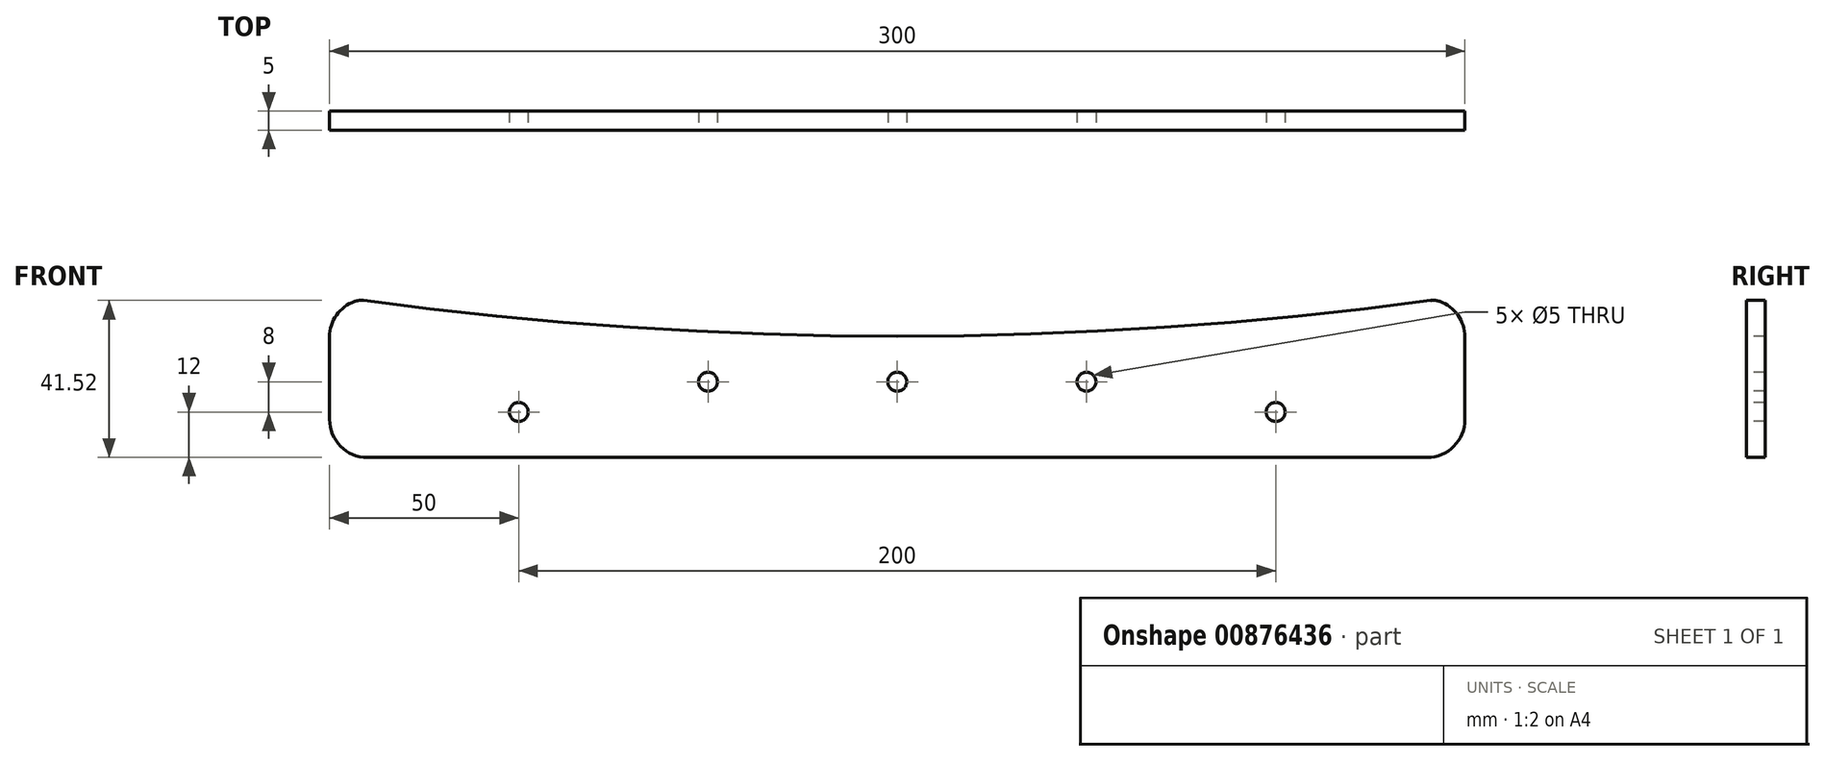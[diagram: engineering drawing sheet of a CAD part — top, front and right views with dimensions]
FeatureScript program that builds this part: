
annotation { "Feature Type Name" : "Feature", "Feature Type Description" : "" }
export const myFeature = defineFeature(function(context is Context, id is Id, definition is map)
    precondition{}
    {
        {
            var Q0;
            Q0=qCreatedBy(makeId("Front.planeOp"),FACE);
            var sketch = newSketch(context, id + "F0", { "sketchPlane" : qUnion([Q0])});
            skLineSegment(sketch, "E0", {"start": v(0, 0) * mm, "end": v(150, 0) * mm});
            skLineSegment(sketch, "E1", {"start": v(150, 0) * mm, "end": v(150, 40) * mm});
            skLineSegment(sketch, "E2", {"start": v(150, 40) * mm, "end": v(50.33, 60) * mm});
            skLineSegment(sketch, "E3", {"start": v(0, 70.22) * mm, "end": v(0, 0) * mm, "construction": true});
            skArc(sketch, "E4", {"start": v(50.33, 60) * mm, "mid": v(25.29, 63.75) * mm, "end": v(0, 65) * mm});
            skLineSegment(sketch, "E5", {"start": v(0, 65) * mm, "end": v(29, 65) * mm, "construction": true});
            skArc(sketch, "E6.MirrorCS", {"start": v(-50.33, 60) * mm, "mid": v(-25.29, 63.75) * mm, "end": v(0, 65) * mm});
            skLineSegment(sketch, "E7.MirrorCS", {"start": v(-150, 40) * mm, "end": v(-50.33, 60) * mm});
            skLineSegment(sketch, "E8.MirrorCS", {"start": v(-150, 0) * mm, "end": v(-150, 40) * mm});
            skLineSegment(sketch, "E9.MirrorCS", {"start": v(0, 0) * mm, "end": v(-150, 0) * mm});
            skSolve(sketch);
        }
        {
            var Q0;
            Q0=makeQuery(id+"F0.imprint","IMPRINT",FACE,{"disambiguationData":[TD([[makeQuery(id+"F0.imprint","IMPRINT",EDGE,{"derivedFrom":sQuery(id+"F0.wireOp",EDGE,"E0")}),1.0]])]});
            extrude(context, id + "F1", {"entities" : qUnion([Q0]), "depth" : 5 * mm, "offsetDistance" : 25 * mm});
        }
        {
            var Q0;
            Q0=makeQuery(id+"F1.opExtrude","SWEPT_EDGE",EDGE,{"disambiguationData":[OSD([sQuery(id+"F0.wireOp",EDGE,"E1"),sQuery(id+"F0.wireOp",EDGE,"E2")])]});
            var Q1;
            Q1=makeQuery(id+"F1.opExtrude","SWEPT_EDGE",EDGE,{"disambiguationData":[OSD([sQuery(id+"F0.wireOp",EDGE,"E7.MirrorCS"),sQuery(id+"F0.wireOp",EDGE,"E8.MirrorCS")])]});
            fillet(context, id + "F2", {"entities" : qUnion([Q0, Q1]), "radius" : 10 * mm, "tangentPropagation" : true, "allowEdgeOverflow" : false});
        }
        {
            var Q0;
            Q0=makeQuery(id+"F1.opExtrude","SWEPT_EDGE",EDGE,{"disambiguationData":[OSD([sQuery(id+"F0.wireOp",EDGE,"E8.MirrorCS"),sQuery(id+"F0.wireOp",EDGE,"E9.MirrorCS")])]});
            var Q1;
            Q1=makeQuery(id+"F1.opExtrude","SWEPT_EDGE",EDGE,{"disambiguationData":[OSD([sQuery(id+"F0.wireOp",EDGE,"E0"),sQuery(id+"F0.wireOp",EDGE,"E1")])]});
            fillet(context, id + "F3", {"entities" : qUnion([Q0, Q1]), "radius" : 10 * mm, "tangentPropagation" : true, "allowEdgeOverflow" : false});
        }
        {
            var Q0;
            Q0=makeQuery(id+"F1.opExtrude","CAP_FACE",FACE,{"disambiguationData":[OSD([sQuery(id+"F0.wireOp",EDGE,"E0"),sQuery(id+"F0.wireOp",EDGE,"E1"),sQuery(id+"F0.wireOp",EDGE,"E2"),sQuery(id+"F0.wireOp",EDGE,"E4"),sQuery(id+"F0.wireOp",EDGE,"E6.MirrorCS"),sQuery(id+"F0.wireOp",EDGE,"E7.MirrorCS"),sQuery(id+"F0.wireOp",EDGE,"E8.MirrorCS"),sQuery(id+"F0.wireOp",EDGE,"E9.MirrorCS")])],"isStart":false});
            var sketch = newSketch(context, id + "F4", { "sketchPlane" : qUnion([Q0])});
            skCircle(sketch, "E10", {"center": v(-50, 20) * mm, "radius": 2.5 * mm});
            skCircle(sketch, "E11", {"center": v(50, 20) * mm, "radius": 2.5 * mm});
            skCircle(sketch, "E12", {"center": v(0, 20) * mm, "radius": 2.5 * mm});
            skSolve(sketch);
        }
        {
            var Q0;
            Q0 = qSketchRegion(id + "F4", true);
            extrude(context, id + "F5", {"entities" : qUnion([Q0]), "operationType" : NewBodyOperationType.REMOVE, "oppositeDirection" : true, "depth" : 25 * mm, "offsetDistance" : 25 * mm});
        }
        {
            var Q0;
            Q0=makeQuery(id+"F1.opExtrude","CAP_FACE",FACE,{"disambiguationData":[OSD([sQuery(id+"F0.wireOp",EDGE,"E0"),sQuery(id+"F0.wireOp",EDGE,"E1"),sQuery(id+"F0.wireOp",EDGE,"E2"),sQuery(id+"F0.wireOp",EDGE,"E4"),sQuery(id+"F0.wireOp",EDGE,"E6.MirrorCS"),sQuery(id+"F0.wireOp",EDGE,"E7.MirrorCS"),sQuery(id+"F0.wireOp",EDGE,"E8.MirrorCS"),sQuery(id+"F0.wireOp",EDGE,"E9.MirrorCS")])],"isStart":false});
            var sketch = newSketch(context, id + "F6", { "sketchPlane" : qUnion([Q0])});
            skCircle(sketch, "E13", {"center": v(-100, 12) * mm, "radius": 2.5 * mm});
            skLineSegment(sketch, "E14", {"start": v(-50, 20) * mm, "end": v(-50, -7.26) * mm, "construction": true});
            skCircle(sketch, "E15.MirrorC", {"center": v(100, 12) * mm, "radius": 2.5 * mm});
            skCircle(sketch, "E16.0", {"center": v(50, 20) * mm, "radius": 2.5 * mm});
            skSolve(sketch);
        }
        {
            var Q0;
            Q0 = qSketchRegion(id + "F6", true);
            extrude(context, id + "F7", {"entities" : qUnion([Q0]), "operationType" : NewBodyOperationType.REMOVE, "oppositeDirection" : true, "depth" : 25 * mm, "offsetDistance" : 25 * mm});
        }
        {
            var Q0;
            Q0=makeQuery(id+"F1.opExtrude","CAP_FACE",FACE,{"disambiguationData":[OSD([sQuery(id+"F0.wireOp",EDGE,"E0"),sQuery(id+"F0.wireOp",EDGE,"E1"),sQuery(id+"F0.wireOp",EDGE,"E2"),sQuery(id+"F0.wireOp",EDGE,"E4"),sQuery(id+"F0.wireOp",EDGE,"E6.MirrorCS"),sQuery(id+"F0.wireOp",EDGE,"E7.MirrorCS"),sQuery(id+"F0.wireOp",EDGE,"E8.MirrorCS"),sQuery(id+"F0.wireOp",EDGE,"E9.MirrorCS")])],"isStart":false});
            var sketch = newSketch(context, id + "F8", { "sketchPlane" : qUnion([Q0])});
            skArc(sketch, "E17", {"start": v(-141.97, 41.61) * mm, "mid": v(0, 32.03) * mm, "end": v(141.97, 41.61) * mm});
            skLineSegment(sketch, "E18", {"start": v(-141.97, 41.61) * mm, "end": v(-141.97, 76.7) * mm});
            skLineSegment(sketch, "E19", {"start": v(-141.97, 76.7) * mm, "end": v(141.97, 76.7) * mm});
            skLineSegment(sketch, "E20", {"start": v(141.97, 76.7) * mm, "end": v(141.97, 41.61) * mm});
            skSolve(sketch);
        }
        {
            var Q0;
            Q0=makeQuery(id+"F8.imprint","IMPRINT",FACE,{"disambiguationData":[TD([[makeQuery(id+"F8.imprint","IMPRINT",EDGE,{"derivedFrom":sQuery(id+"F8.wireOp",EDGE,"E18")}),-1.0]])]});
            var Q1;
            Q1=makeQuery(id+"F8.imprint","IMPRINT",FACE,{"disambiguationData":[TD([[makeQuery(id+"F8.imprint","IMPRINT",EDGE,{"derivedFrom":sQuery(id+"F8.wireOp",EDGE,"E17")}),1.0]])]});
            extrude(context, id + "F9", {"entities" : qUnion([Q0, Q1]), "operationType" : NewBodyOperationType.REMOVE, "oppositeDirection" : true, "depth" : 25 * mm, "offsetDistance" : 25 * mm});
        }
        {
            var Q0;
            {var subQ0=sQuery(id+"F0.wireOp",EDGE,"E8.MirrorCS");var subQ1=sQuery(id+"F0.wireOp",EDGE,"E7.MirrorCS");Q0=makeQuery(id+"F9.boolean.opBoolean","MERGE",EDGE,{"derivedFrom":[makeQuery(id+"F2.opFillet","BLEND_EDGE",EDGE,{"blendedFrom":[makeQuery(id+"F1.opExtrude","SWEPT_EDGE",EDGE,{"disambiguationData":[OSD([subQ1,subQ0])]}),makeQuery(id+"F1.opExtrude","SWEPT_FACE",FACE,{"disambiguationData":[OSD([subQ1])]})],"blendedInto":[makeQuery(id+"F1.opExtrude","SWEPT_FACE",FACE,{"disambiguationData":[OSD([subQ1])]})]})],"fromTools":[makeQuery(id+"F9.opExtrude","SWEPT_EDGE",EDGE,{"disambiguationData":[OSD([sQuery(id+"F0.wireOp",EDGE,"E0"),sQuery(id+"F0.wireOp",EDGE,"E1"),sQuery(id+"F0.wireOp",EDGE,"E2"),sQuery(id+"F0.wireOp",EDGE,"E4"),sQuery(id+"F0.wireOp",EDGE,"E6.MirrorCS"),subQ1,subQ0,sQuery(id+"F0.wireOp",EDGE,"E9.MirrorCS"),sQuery(id+"F8.wireOp",EDGE,"E17"),sQuery(id+"F8.wireOp",EDGE,"E18")])]})]});}
            var Q1;
            {var subQ0=sQuery(id+"F0.wireOp",EDGE,"E2");var subQ1=sQuery(id+"F0.wireOp",EDGE,"E1");Q1=makeQuery(id+"F9.boolean.opBoolean","MERGE",EDGE,{"derivedFrom":[makeQuery(id+"F2.opFillet","BLEND_EDGE",EDGE,{"blendedFrom":[makeQuery(id+"F1.opExtrude","SWEPT_EDGE",EDGE,{"disambiguationData":[OSD([subQ1,subQ0])]}),makeQuery(id+"F1.opExtrude","SWEPT_FACE",FACE,{"disambiguationData":[OSD([subQ0])]})],"blendedInto":[makeQuery(id+"F1.opExtrude","SWEPT_FACE",FACE,{"disambiguationData":[OSD([subQ0])]})]})],"fromTools":[makeQuery(id+"F9.opExtrude","SWEPT_EDGE",EDGE,{"disambiguationData":[OSD([sQuery(id+"F0.wireOp",EDGE,"E0"),subQ1,subQ0,sQuery(id+"F0.wireOp",EDGE,"E4"),sQuery(id+"F0.wireOp",EDGE,"E6.MirrorCS"),sQuery(id+"F0.wireOp",EDGE,"E7.MirrorCS"),sQuery(id+"F0.wireOp",EDGE,"E8.MirrorCS"),sQuery(id+"F0.wireOp",EDGE,"E9.MirrorCS"),sQuery(id+"F8.wireOp",EDGE,"E17"),sQuery(id+"F8.wireOp",EDGE,"E20")])]})]});}
            fillet(context, id + "F10", {"entities" : qUnion([Q0, Q1]), "radius" : 5 * mm, "tangentPropagation" : true, "allowEdgeOverflow" : false});
        }
    });
